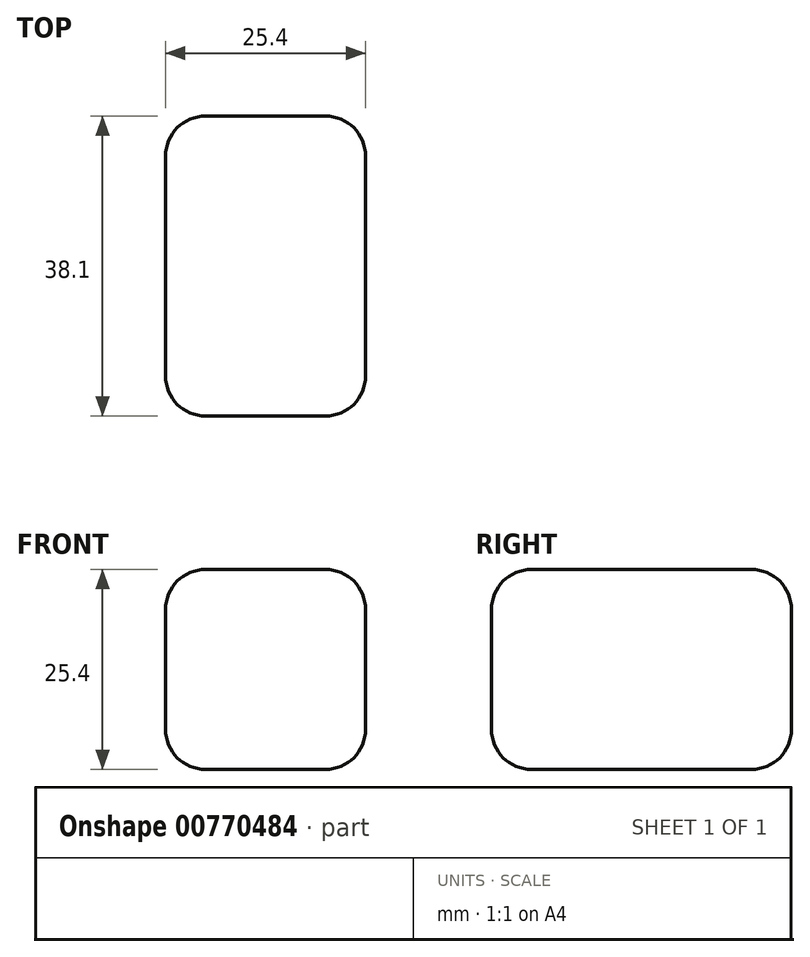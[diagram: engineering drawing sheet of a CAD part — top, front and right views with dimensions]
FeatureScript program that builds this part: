
annotation { "Feature Type Name" : "Feature", "Feature Type Description" : "" }
export const myFeature = defineFeature(function(context is Context, id is Id, definition is map)
    precondition{}
    {
        {
            var Q0;
            Q0=qCreatedBy(makeId("Top.planeOp"),FACE);
            var sketch = newSketch(context, id + "F0", { "sketchPlane" : qUnion([Q0])});
            skLineSegment(sketch, "E0.bottom", {"start": v(12.7, -19.05) * mm, "end": v(-12.7, -19.05) * mm});
            skLineSegment(sketch, "E0.top", {"start": v(12.7, 19.05) * mm, "end": v(-12.7, 19.05) * mm});
            skLineSegment(sketch, "E0.left", {"start": v(12.7, -19.05) * mm, "end": v(12.7, 19.05) * mm});
            skLineSegment(sketch, "E0.right", {"start": v(-12.7, -19.05) * mm, "end": v(-12.7, 19.05) * mm});
            skPoint(sketch, "E0.middle", {"position": v(0, 0) * mm});
            skSolve(sketch);
        }
        {
            var Q0;
            Q0=makeQuery(id+"F0.imprint","IMPRINT",FACE,{"disambiguationData":[TD([[makeQuery(id+"F0.imprint","IMPRINT",EDGE,{"derivedFrom":sQuery(id+"F0.wireOp",EDGE,"E0.bottom")}),-1.0]])]});
            extrude(context, id + "F1", {"entities" : qUnion([Q0]), "depth" : 25.4 * mm, "offsetDistance" : 25.4 * mm});
        }
        {
            var Q0;
            Q0 = qSketchRegion(id + "F0", true);
            extrude(context, id + "F2", {"entities" : qUnion([Q0]), "operationType" : NewBodyOperationType.ADD, "depth" : 25.4 * mm, "offsetDistance" : 25.4 * mm});
        }
        {
            var Q0;
            Q0=makeQuery(id+"F1.opExtrude","CAP_EDGE",EDGE,{"disambiguationData":[OSD([sQuery(id+"F0.wireOp",EDGE,"E0.right")])],"isStart":false});
            var Q1;
            Q1=makeQuery(id+"F1.opExtrude","CAP_EDGE",EDGE,{"disambiguationData":[OSD([sQuery(id+"F0.wireOp",EDGE,"E0.left")])],"isStart":false});
            var Q2;
            Q2=makeQuery(id+"F1.opExtrude","CAP_EDGE",EDGE,{"disambiguationData":[OSD([sQuery(id+"F0.wireOp",EDGE,"E0.right")])],"isStart":true});
            var Q3;
            Q3=makeQuery(id+"F1.opExtrude","CAP_EDGE",EDGE,{"disambiguationData":[OSD([sQuery(id+"F0.wireOp",EDGE,"E0.left")])],"isStart":true});
            fillet(context, id + "F3", {"entities" : qUnion([Q0, Q1, Q2, Q3]), "radius" : 5.08 * mm, "tangentPropagation" : true, "allowEdgeOverflow" : false});
        }
        {
            var Q0;
            Q0=makeQuery(id+"F1.opExtrude","CAP_EDGE",EDGE,{"disambiguationData":[OSD([sQuery(id+"F0.wireOp",EDGE,"E0.bottom")])],"isStart":false});
            var Q1;
            Q1=makeQuery(id+"F1.opExtrude","SWEPT_EDGE",EDGE,{"disambiguationData":[OSD([sQuery(id+"F0.wireOp",EDGE,"E0.bottom"),sQuery(id+"F0.wireOp",EDGE,"E0.right")])]});
            var Q2;
            Q2=makeQuery(id+"F1.opExtrude","SWEPT_EDGE",EDGE,{"disambiguationData":[OSD([sQuery(id+"F0.wireOp",EDGE,"E0.bottom"),sQuery(id+"F0.wireOp",EDGE,"E0.left")])]});
            var Q3;
            Q3=makeQuery(id+"F1.opExtrude","SWEPT_EDGE",EDGE,{"disambiguationData":[OSD([sQuery(id+"F0.wireOp",EDGE,"E0.top"),sQuery(id+"F0.wireOp",EDGE,"E0.right")])]});
            var Q4;
            Q4=makeQuery(id+"F1.opExtrude","SWEPT_EDGE",EDGE,{"disambiguationData":[OSD([sQuery(id+"F0.wireOp",EDGE,"E0.top"),sQuery(id+"F0.wireOp",EDGE,"E0.left")])]});
            fillet(context, id + "F4", {"entities" : qUnion([Q0, Q1, Q2, Q3, Q4]), "radius" : 5.08 * mm, "tangentPropagation" : true, "allowEdgeOverflow" : false});
        }
    });
